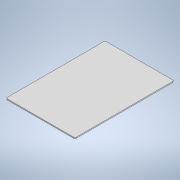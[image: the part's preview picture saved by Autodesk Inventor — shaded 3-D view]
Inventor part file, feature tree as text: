
AUTODESK INVENTOR PART (.ipt)
format: ipt  version: 2021 (Build 250183000, 183)  size: 98,816 bytes
history: native  units: mm
features: other x1, extrude x1, fillet x1, sketch x1
ambient origin geometry x8: Origin, YZ Plane, XZ Plane, XY Plane, X Axis, Y Axis, Z Axis, Center Point
bodies: Body1 (feature_tree)
feature tree (4):
  other  "實體1"
  extrude  "擠出1"  Depth=320.0mm
  fillet  "圓角1"  Radius=460.0mm
  sketch  "草圖1"
